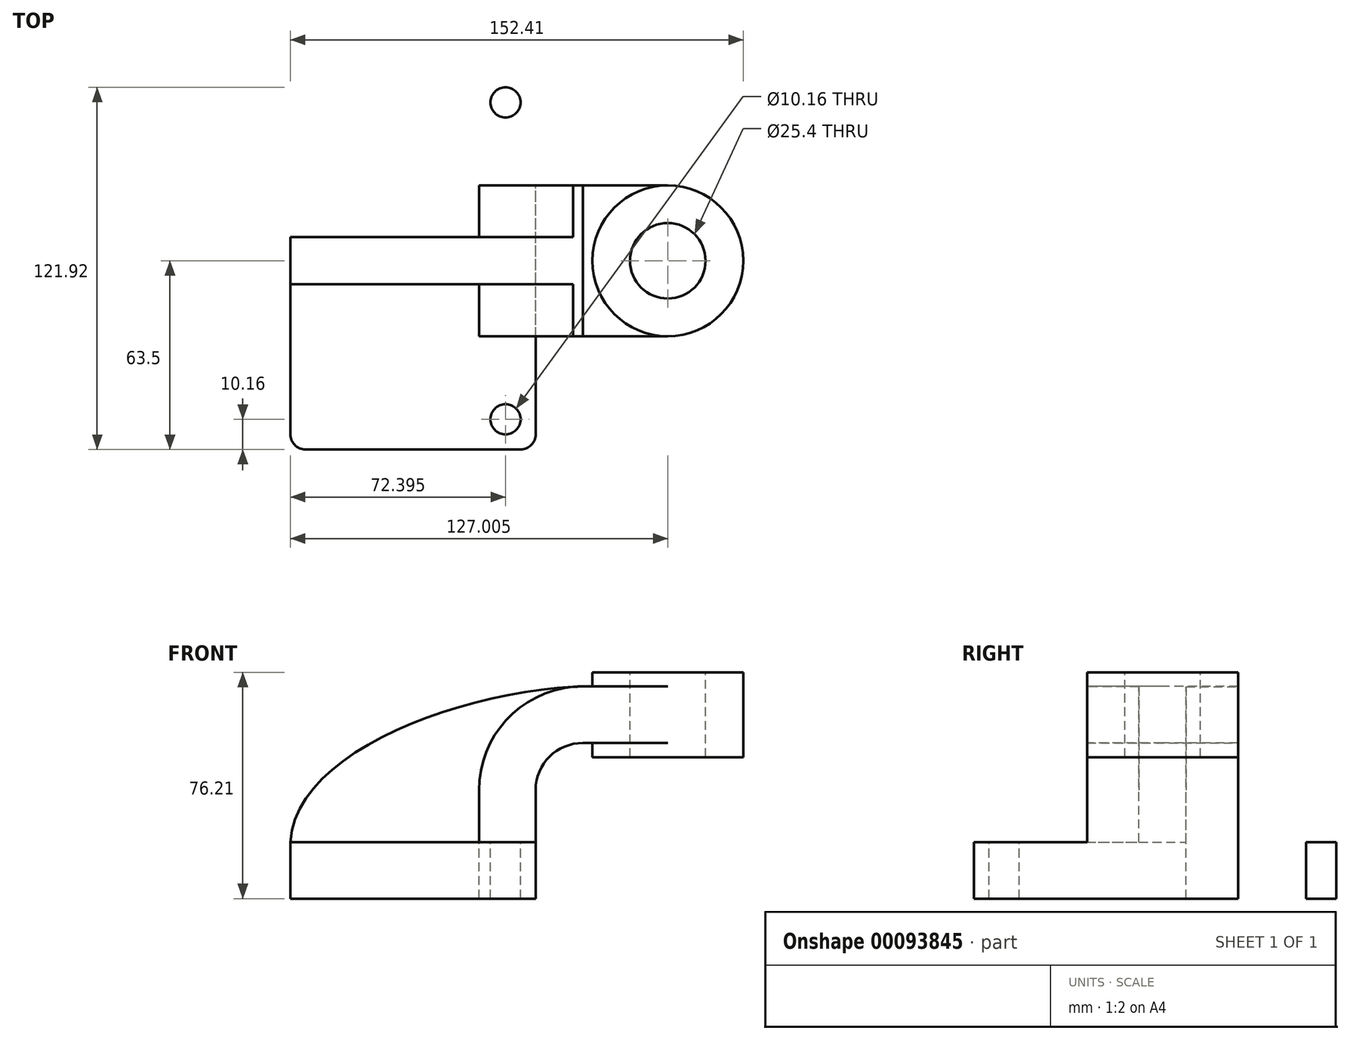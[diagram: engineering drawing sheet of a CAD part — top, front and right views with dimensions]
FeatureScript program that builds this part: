
annotation { "Feature Type Name" : "Feature", "Feature Type Description" : "" }
export const myFeature = defineFeature(function(context is Context, id is Id, definition is map)
    precondition{}
    {
        {
            var Q0;
            Q0=qCreatedBy(makeId("Front.planeOp"),FACE);
            var sketch = newSketch(context, id + "F0", { "sketchPlane" : qUnion([Q0])});
            skLineSegment(sketch, "E0.rect.bottom", {"start": v(-41.28, 9.52) * mm, "end": v(41.28, 9.52) * mm});
            skLineSegment(sketch, "E0.rect.top", {"start": v(-41.28, -9.52) * mm, "end": v(41.28, -9.52) * mm});
            skLineSegment(sketch, "E0.rect.left", {"start": v(-41.28, 9.52) * mm, "end": v(-41.28, -9.52) * mm});
            skLineSegment(sketch, "E0.rect.right", {"start": v(41.28, 9.52) * mm, "end": v(41.28, -9.52) * mm});
            skPoint(sketch, "E0.rect.middle", {"position": v(0, 0) * mm});
            skLineSegment(sketch, "E1", {"start": v(41.28, 9.52) * mm, "end": v(41.28, 27) * mm});
            skArc(sketch, "E2", {"start": v(41.28, 27) * mm, "mid": v(45.92, 38.23) * mm, "end": v(57.15, 42.88) * mm});
            skLineSegment(sketch, "E3", {"start": v(57.15, 42.88) * mm, "end": v(85.72, 42.88) * mm});
            skLineSegment(sketch, "E4.rect.bottom", {"start": v(60.32, 38.1) * mm, "end": v(111.12, 38.1) * mm});
            skLineSegment(sketch, "E4.rect.top", {"start": v(60.32, 66.68) * mm, "end": v(111.12, 66.68) * mm});
            skLineSegment(sketch, "E4.rect.left", {"start": v(60.32, 38.1) * mm, "end": v(60.32, 66.68) * mm});
            skLineSegment(sketch, "E4.rect.right", {"start": v(111.13, 38.1) * mm, "end": v(111.12, 66.68) * mm});
            skPoint(sketch, "E4.rect.middle", {"position": v(85.72, 52.39) * mm});
            skLineSegment(sketch, "E5.0", {"start": v(57.15, 61.93) * mm, "end": v(85.72, 61.93) * mm});
            skArc(sketch, "E5.1", {"start": v(22.23, 27) * mm, "mid": v(32.45, 51.7) * mm, "end": v(57.15, 61.93) * mm});
            skLineSegment(sketch, "E5.2", {"start": v(22.23, 9.52) * mm, "end": v(22.23, 27) * mm});
            skLineSegment(sketch, "E6", {"start": v(85.72, 38.1) * mm, "end": v(85.72, 66.68) * mm});
            skFitSpline(sketch, "E7", {"points": [v(-41.28, 9.53) * mm, v(57.15, 61.93) * mm], "startDerivative": vector(5.2, 92.34) * mm, "endDerivative": vector(120.92, 4.22) * mm});
            skSolve(sketch);
        }
        {
            var Q0;
            Q0=makeQuery(id+"F0.imprint","IMPRINT",FACE,{"disambiguationData":[TD([[makeQuery(id+"F0.imprint","IMPRINT",EDGE,{"derivedFrom":sQuery(id+"F0.wireOp",EDGE,"E0.rect.top")}),1.0]])]});
            extrude(context, id + "F1", {"entities" : qUnion([Q0]), "endBound" : BoundingType.SYMMETRIC, "depth" : 127 * mm});
        }
        {
            var Q0;
            {var subQ9=sQuery(id+"F0.wireOp",EDGE,"E1");Q0=makeQuery(id+"F0.imprint","IMPRINT",FACE,{"disambiguationData":[TD([[makeQuery(id+"F0.imprint","IMPRINT",EDGE,{"derivedFrom":subQ9}),1.0]])]});}
            var Q1;
            {var subQ0=sQuery(id+"F0.wireOp",EDGE,"E6");var subQ1=sQuery(id+"F0.wireOp",EDGE,"E3");var subQ2=makeQuery(id+"F0.imprint","INTERSECT",VERTEX,{"derivedFrom":[subQ1,subQ0]});Q1=makeQuery(id+"F0.imprint","IMPRINT",FACE,{"disambiguationData":[TD([[makeQuery(id+"F0.imprint","IMPRINT",EDGE,{"disambiguationData":[TD([[subQ2,1.0]])],"derivedFrom":subQ1}),1.0]])]});}
            extrude(context, id + "F2", {"entities" : qUnion([Q0, Q1]), "operationType" : NewBodyOperationType.ADD, "endBound" : BoundingType.SYMMETRIC, "depth" : 50.8 * mm});
        }
        {
            var Q0;
            {var subQ3=sQuery(id+"F0.wireOp",EDGE,"E5.2");Q0=makeQuery(id+"F0.imprint","IMPRINT",FACE,{"disambiguationData":[TD([[makeQuery(id+"F0.imprint","IMPRINT",EDGE,{"derivedFrom":subQ3}),1.0]])]});}
            extrude(context, id + "F3", {"entities" : qUnion([Q0]), "operationType" : NewBodyOperationType.ADD, "endBound" : BoundingType.SYMMETRIC, "depth" : 15.88 * mm});
        }
        {
            var Q0;
            {var subQ5=sQuery(id+"F0.wireOp",EDGE,"E4.rect.right");Q0=makeQuery(id+"F0.imprint","IMPRINT",FACE,{"disambiguationData":[TD([[makeQuery(id+"F0.imprint","IMPRINT",EDGE,{"derivedFrom":subQ5}),1.0]])]});}
            var Q1;
            Q1=sQuery(id+"F0.wireOp",EDGE,"E6");
            revolve(context, id + "F4", {"operationType" : NewBodyOperationType.ADD, "entities" : qUnion([Q0]), "axis" : qUnion([Q1]), "revolveType" : RevolveType.FULL});
        }
        {
            var Q0;
            Q0=makeQuery(id+"F1.opExtrude","CAP_EDGE",EDGE,{"disambiguationData":[OSD([sQuery(id+"F0.wireOp",EDGE,"E0.rect.right")])],"isStart":false});
            var Q1;
            Q1=makeQuery(id+"F1.opExtrude","CAP_EDGE",EDGE,{"disambiguationData":[OSD([sQuery(id+"F0.wireOp",EDGE,"E0.rect.left")])],"isStart":false});
            var Q2;
            Q2=makeQuery(id+"F1.opExtrude","CAP_EDGE",EDGE,{"disambiguationData":[OSD([sQuery(id+"F0.wireOp",EDGE,"E0.rect.right")])],"isStart":true});
            var Q3;
            Q3=makeQuery(id+"F1.opExtrude","CAP_EDGE",EDGE,{"disambiguationData":[OSD([sQuery(id+"F0.wireOp",EDGE,"E0.rect.left")])],"isStart":true});
            fillet(context, id + "F5", {"entities" : qUnion([Q0, Q1, Q2, Q3]), "radius" : 5.08 * mm, "tangentPropagation" : true, "allowEdgeOverflow" : false});
        }
        {
            var Q0;
            {var subQ4=sQuery(id+"F0.wireOp",EDGE,"E0.rect.bottom");var subQ5=sQuery(id+"F0.wireOp",EDGE,"E0.rect.right");var subQ6=sQuery(id+"F0.wireOp",EDGE,"E0.rect.left");Q0=makeQuery(id+"F3.boolean.opBoolean","SPLIT",FACE,{"disambiguationData":[TD([makeQuery(id+"F1.opExtrude","CAP_FACE",FACE,{"disambiguationData":[OSD([subQ4,sQuery(id+"F0.wireOp",EDGE,"E0.rect.top"),subQ6,subQ5])],"isStart":true})])],"derivedFrom":makeQuery(id+"F1.opExtrude","SWEPT_FACE",FACE,{"disambiguationData":[OSD([subQ4])]})});}
            var sketch = newSketch(context, id + "F6", { "sketchPlane" : qUnion([Q0])});
            skCircle(sketch, "E8", {"center": v(-31.12, 53.34) * mm, "radius": 5.08 * mm});
            skCircle(sketch, "E9.MirrorC", {"center": v(31.12, 53.34) * mm, "radius": 5.08 * mm});
            skCircle(sketch, "E10.MirrorC", {"center": v(-31.12, -53.34) * mm, "radius": 5.08 * mm});
            skCircle(sketch, "E11.MirrorC", {"center": v(31.12, -53.34) * mm, "radius": 5.08 * mm});
            skSolve(sketch);
        }
        {
            var Q0;
            Q0=makeQuery(id+"F6.imprint","IMPRINT",FACE,{"disambiguationData":[TD([[makeQuery(id+"F6.imprint","IMPRINT",EDGE,{"derivedFrom":sQuery(id+"F6.wireOp",EDGE,"E10.MirrorC")}),-1.0]])]});
            var Q1;
            Q1=makeQuery(id+"F6.imprint","IMPRINT",FACE,{"disambiguationData":[TD([[makeQuery(id+"F6.imprint","IMPRINT",EDGE,{"derivedFrom":sQuery(id+"F6.wireOp",EDGE,"E11.MirrorC")}),1.0]])]});
            var Q2;
            Q2=makeQuery(id+"F6.imprint","IMPRINT",FACE,{"disambiguationData":[TD([[makeQuery(id+"F6.imprint","IMPRINT",EDGE,{"derivedFrom":sQuery(id+"F6.wireOp",EDGE,"E9.MirrorC")}),-1.0]])]});
            var Q3;
            Q3=makeQuery(id+"F6.imprint","IMPRINT",FACE,{"disambiguationData":[TD([[makeQuery(id+"F6.imprint","IMPRINT",EDGE,{"derivedFrom":sQuery(id+"F6.wireOp",EDGE,"E8")}),1.0]])]});
            extrude(context, id + "F7", {"entities" : qUnion([Q0, Q1, Q2, Q3]), "operationType" : NewBodyOperationType.REMOVE, "endBound" : BoundingType.UP_TO_NEXT, "oppositeDirection" : true, "depth" : 25.4 * mm});
        }
        {
            var Q0;
            Q0=makeQuery(id+"F4.opRevolve","SWEPT_FACE",FACE,{"disambiguationData":[OSD([sQuery(id+"F0.wireOp",EDGE,"E4.rect.top")])]});
            var sketch = newSketch(context, id + "F8", { "sketchPlane" : qUnion([Q0])});
            skCircle(sketch, "E12.0", {"center": v(85.72, 0) * mm, "radius": 12.7 * mm});
            skSolve(sketch);
        }
        {
            var Q0;
            Q0=makeQuery(id+"F8.imprint","IMPRINT",FACE,{"disambiguationData":[TD([[makeQuery(id+"F8.imprint","IMPRINT",EDGE,{"derivedFrom":sQuery(id+"F8.wireOp",EDGE,"E12.0")}),1.0]])]});
            var Q1;
            Q1=sQuery(id+"F8.wireOp",EDGE,"E12.0");
            extrude(context, id + "F9", {"entities" : qUnion([Q0]), "operationType" : NewBodyOperationType.REMOVE, "surfaceEntities" : qUnion([Q1]), "endBound" : BoundingType.UP_TO_NEXT, "oppositeDirection" : true, "depth" : 25.4 * mm});
        }
    });
